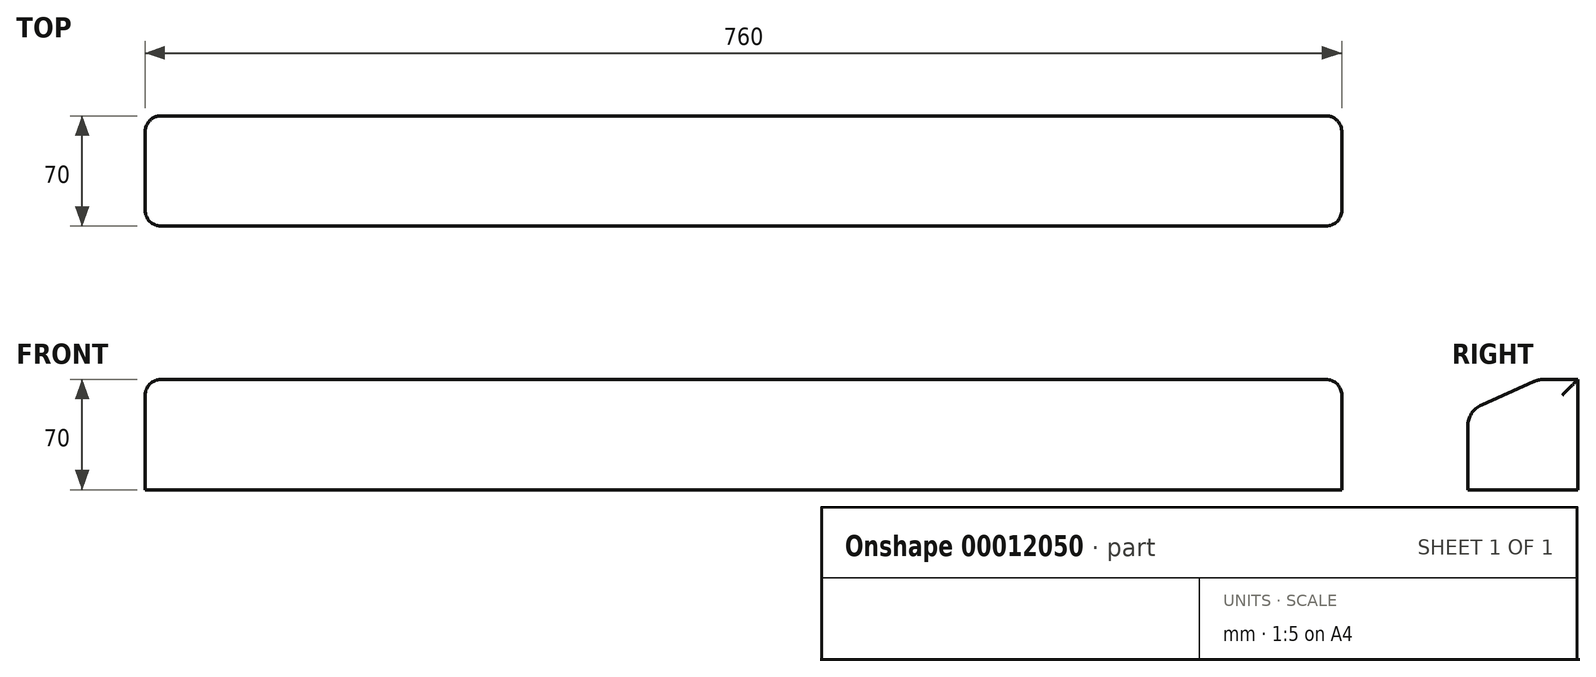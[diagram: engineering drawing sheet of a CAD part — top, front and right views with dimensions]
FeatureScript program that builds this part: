
annotation { "Feature Type Name" : "Feature", "Feature Type Description" : "" }
export const myFeature = defineFeature(function(context is Context, id is Id, definition is map)
    precondition{}
    {
        {
            var Q0;
            Q0=qCreatedBy(makeId("Right.planeOp"),FACE);
            var sketch = newSketch(context, id + "F0", { "sketchPlane" : qUnion([Q0])});
            skLineSegment(sketch, "E0", {"start": v(0, 0) * mm, "end": v(0, 70) * mm});
            skLineSegment(sketch, "E1", {"start": v(0, 70) * mm, "end": v(-21.82, 70) * mm});
            skLineSegment(sketch, "E2", {"start": v(-27.9, 68.7) * mm, "end": v(-61.1, 53.96) * mm});
            skLineSegment(sketch, "E3", {"start": v(-70, 40.25) * mm, "end": v(-70, 0) * mm});
            skLineSegment(sketch, "E4", {"start": v(-70, 0) * mm, "end": v(0, 0) * mm});
            skPoint(sketch, "E5.visualSharp", {"position": v(-70, 50) * mm});
            skArc(sketch, "E5.filletArc", {"start": v(-61.1, 53.96) * mm, "mid": v(-67.58, 48.43) * mm, "end": v(-70, 40.25) * mm});
            skPoint(sketch, "E6.visualSharp", {"position": v(-25, 70) * mm});
            skArc(sketch, "E6.filletArc", {"start": v(-21.82, 70) * mm, "mid": v(-24.93, 69.67) * mm, "end": v(-27.9, 68.7) * mm});
            skLineSegment(sketch, "E7.top", {"start": v(0, 38) * mm, "end": v(-89, 38) * mm, "construction": true});
            skLineSegment(sketch, "E7.right", {"start": v(-89, 0) * mm, "end": v(-89, 38) * mm, "construction": true});
            skLineSegment(sketch, "E8", {"start": v(-63, 38) * mm, "end": v(-63, 76) * mm, "construction": true});
            skLineSegment(sketch, "E9", {"start": v(-63, 76) * mm, "end": v(0, 76) * mm, "construction": true});
            skLineSegment(sketch, "E10", {"start": v(-21.82, 70) * mm, "end": v(-70, 32.56) * mm, "construction": true});
            skSolve(sketch);
        }
        {
            var Q0;
            Q0 = qSketchRegion(id + "F0", true);
            extrude(context, id + "F1", {"entities" : qUnion([Q0]), "depth" : 760 * mm, "symmetric" : true});
        }
        {
            var Q0;
            Q0=makeQuery(id+"F1.opExtrude","CAP_EDGE",EDGE,{"disambiguationData":[OSD([sQuery(id+"F0.wireOp",EDGE,"E1")])],"isStart":true});
            var Q1;
            Q1=makeQuery(id+"F1.opExtrude","CAP_EDGE",EDGE,{"disambiguationData":[OSD([sQuery(id+"F0.wireOp",EDGE,"E6.filletArc")])],"isStart":true});
            var Q2;
            Q2=makeQuery(id+"F1.opExtrude","CAP_EDGE",EDGE,{"disambiguationData":[OSD([sQuery(id+"F0.wireOp",EDGE,"E2")])],"isStart":true});
            var Q3;
            Q3=makeQuery(id+"F1.opExtrude","CAP_EDGE",EDGE,{"disambiguationData":[OSD([sQuery(id+"F0.wireOp",EDGE,"E5.filletArc")])],"isStart":true});
            var Q4;
            Q4=makeQuery(id+"F1.opExtrude","CAP_EDGE",EDGE,{"disambiguationData":[OSD([sQuery(id+"F0.wireOp",EDGE,"E3")])],"isStart":true});
            var Q5;
            Q5=makeQuery(id+"F1.opExtrude","CAP_EDGE",EDGE,{"disambiguationData":[OSD([sQuery(id+"F0.wireOp",EDGE,"E0")])],"isStart":true});
            var Q6;
            Q6=makeQuery(id+"F1.opExtrude","CAP_EDGE",EDGE,{"disambiguationData":[OSD([sQuery(id+"F0.wireOp",EDGE,"E0")])],"isStart":false});
            var Q7;
            Q7=makeQuery(id+"F1.opExtrude","CAP_EDGE",EDGE,{"disambiguationData":[OSD([sQuery(id+"F0.wireOp",EDGE,"E1")])],"isStart":false});
            var Q8;
            Q8=makeQuery(id+"F1.opExtrude","CAP_EDGE",EDGE,{"disambiguationData":[OSD([sQuery(id+"F0.wireOp",EDGE,"E6.filletArc")])],"isStart":false});
            var Q9;
            Q9=makeQuery(id+"F1.opExtrude","CAP_EDGE",EDGE,{"disambiguationData":[OSD([sQuery(id+"F0.wireOp",EDGE,"E2")])],"isStart":false});
            var Q10;
            Q10=makeQuery(id+"F1.opExtrude","CAP_EDGE",EDGE,{"disambiguationData":[OSD([sQuery(id+"F0.wireOp",EDGE,"E5.filletArc")])],"isStart":false});
            var Q11;
            Q11=makeQuery(id+"F1.opExtrude","CAP_EDGE",EDGE,{"disambiguationData":[OSD([sQuery(id+"F0.wireOp",EDGE,"E3")])],"isStart":false});
            fillet(context, id + "F2", {"entities" : qUnion([Q0, Q1, Q2, Q3, Q4, Q5, Q6, Q7, Q8, Q9, Q10, Q11]), "radius" : 10 * mm, "allowEdgeOverflow" : false});
        }
    });
